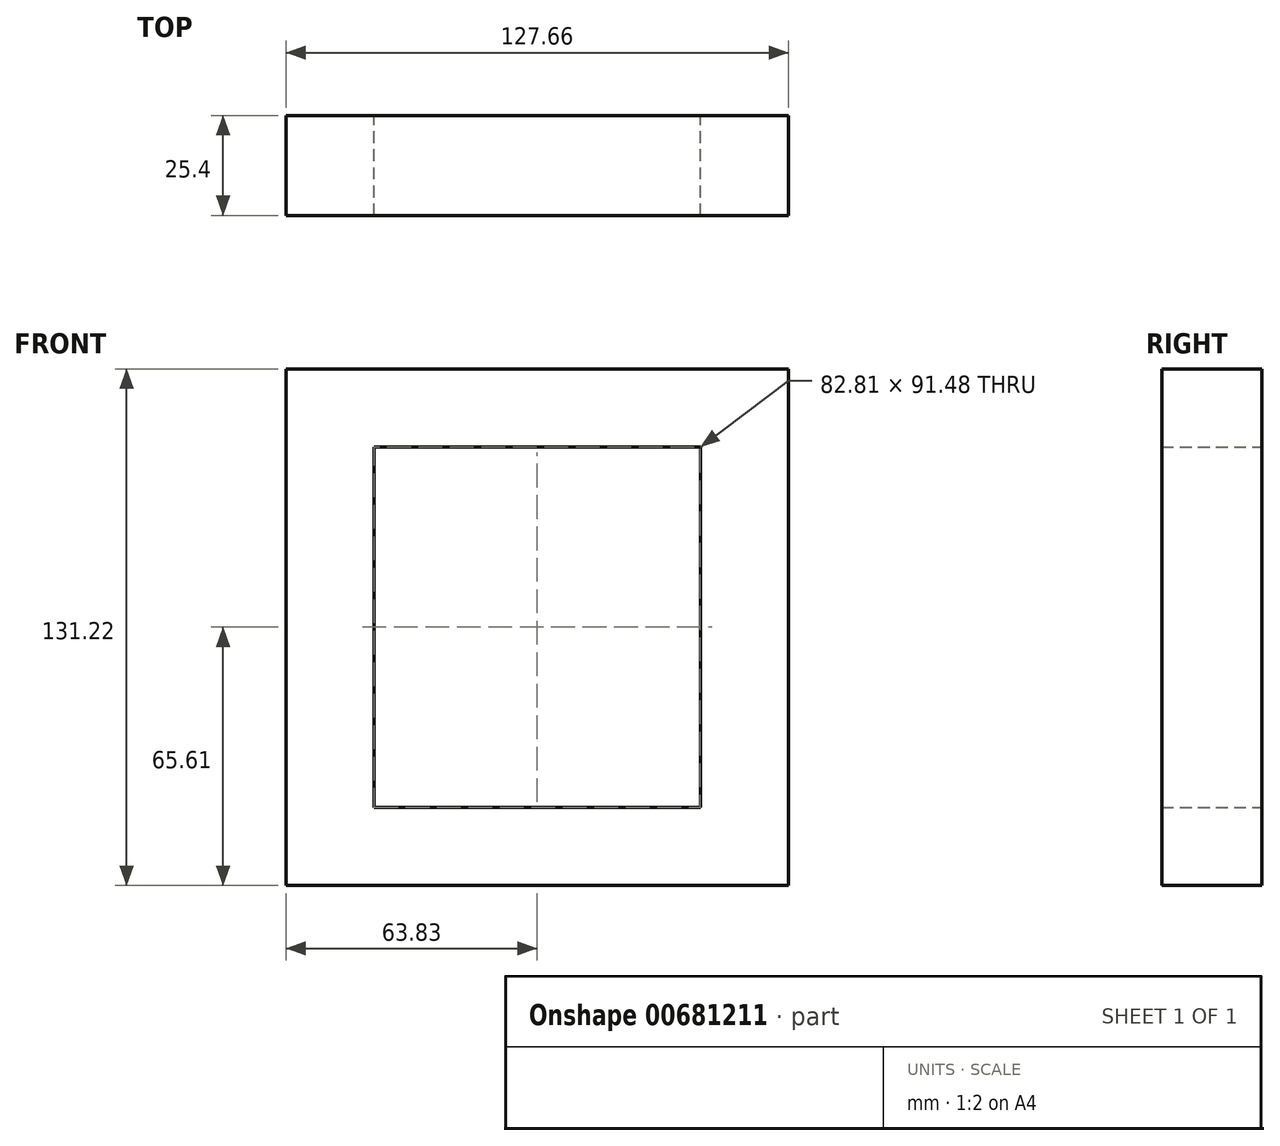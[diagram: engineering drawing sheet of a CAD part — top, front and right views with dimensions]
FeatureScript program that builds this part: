
annotation { "Feature Type Name" : "Feature", "Feature Type Description" : "" }
export const myFeature = defineFeature(function(context is Context, id is Id, definition is map)
    precondition{}
    {
        {
            var Q0;
            Q0=qCreatedBy(makeId("Front.planeOp"),FACE);
            var sketch = newSketch(context, id + "F0", { "sketchPlane" : qUnion([Q0])});
            skLineSegment(sketch, "E0.bottom", {"start": v(41.4, -45.74) * mm, "end": v(-41.4, -45.74) * mm});
            skLineSegment(sketch, "E0.top", {"start": v(41.4, 45.74) * mm, "end": v(-41.4, 45.74) * mm});
            skLineSegment(sketch, "E0.left", {"start": v(41.4, -45.74) * mm, "end": v(41.4, 45.74) * mm});
            skLineSegment(sketch, "E0.right", {"start": v(-41.4, -45.74) * mm, "end": v(-41.4, 45.74) * mm});
            skPoint(sketch, "E0.middle", {"position": v(0, 0) * mm});
            skLineSegment(sketch, "E1.bottom", {"start": v(63.83, -65.61) * mm, "end": v(-63.83, -65.61) * mm});
            skLineSegment(sketch, "E1.top", {"start": v(63.83, 65.61) * mm, "end": v(-63.83, 65.61) * mm});
            skLineSegment(sketch, "E1.left", {"start": v(63.83, -65.61) * mm, "end": v(63.83, 65.61) * mm});
            skLineSegment(sketch, "E1.right", {"start": v(-63.83, -65.61) * mm, "end": v(-63.83, 65.61) * mm});
            skSolve(sketch);
        }
        {
            var Q0;
            Q0=makeQuery(id+"F0.imprint","IMPRINT",FACE,{"disambiguationData":[TD([[makeQuery(id+"F0.imprint","IMPRINT",EDGE,{"derivedFrom":sQuery(id+"F0.wireOp",EDGE,"E0.bottom")}),1.0]])]});
            extrude(context, id + "F1", {"entities" : qUnion([Q0]), "endBound" : BoundingType.SYMMETRIC, "depth" : 25.4 * mm, "offsetDistance" : 25.4 * mm});
        }
    });
